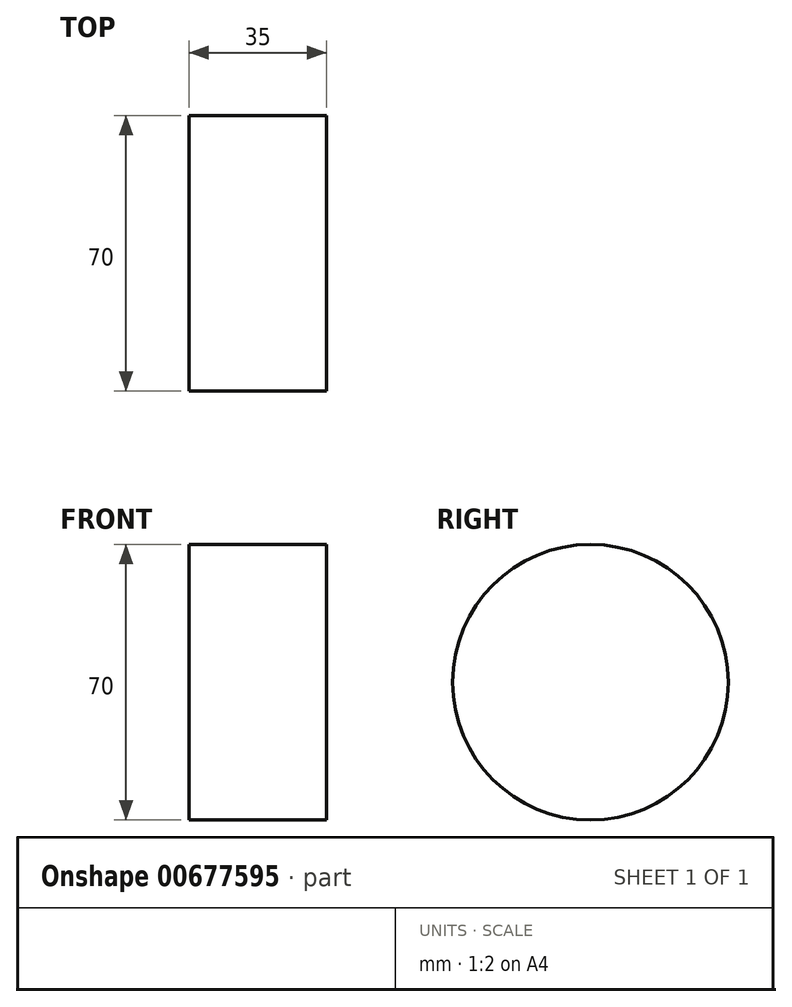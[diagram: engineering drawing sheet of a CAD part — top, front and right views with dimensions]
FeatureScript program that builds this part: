
annotation { "Feature Type Name" : "Feature", "Feature Type Description" : "" }
export const myFeature = defineFeature(function(context is Context, id is Id, definition is map)
    precondition{}
    {
        {
            var Q0;
            Q0=qCreatedBy(makeId("Front.planeOp"),FACE);
            var sketch = newSketch(context, id + "F0", { "sketchPlane" : qUnion([Q0])});
            skLineSegment(sketch, "E0.bottom", {"start": v(0, 0) * mm, "end": v(35, 0) * mm});
            skLineSegment(sketch, "E0.top", {"start": v(0, 35) * mm, "end": v(35, 35) * mm});
            skLineSegment(sketch, "E0.left", {"start": v(0, 0) * mm, "end": v(0, 35) * mm});
            skLineSegment(sketch, "E0.right", {"start": v(35, 0) * mm, "end": v(35, 35) * mm});
            skSolve(sketch);
        }
        {
            var Q0;
            Q0=makeQuery(id+"F0.imprint","IMPRINT",FACE,{"disambiguationData":[TD([[makeQuery(id+"F0.imprint","IMPRINT",EDGE,{"derivedFrom":sQuery(id+"F0.wireOp",EDGE,"E0.bottom")}),1.0]])]});
            var Q1;
            Q1=sQuery(id+"F0.wireOp",EDGE,"E0.bottom");
            revolve(context, id + "F1", {"surfaceOperationType" : NewSurfaceOperationType.NEW, "entities" : qUnion([Q0]), "axis" : qUnion([Q1]), "revolveType" : RevolveType.TWO_DIRECTIONS, "angle" : 360 * degree, "angleBack" : 360 * degree});
        }
    });
